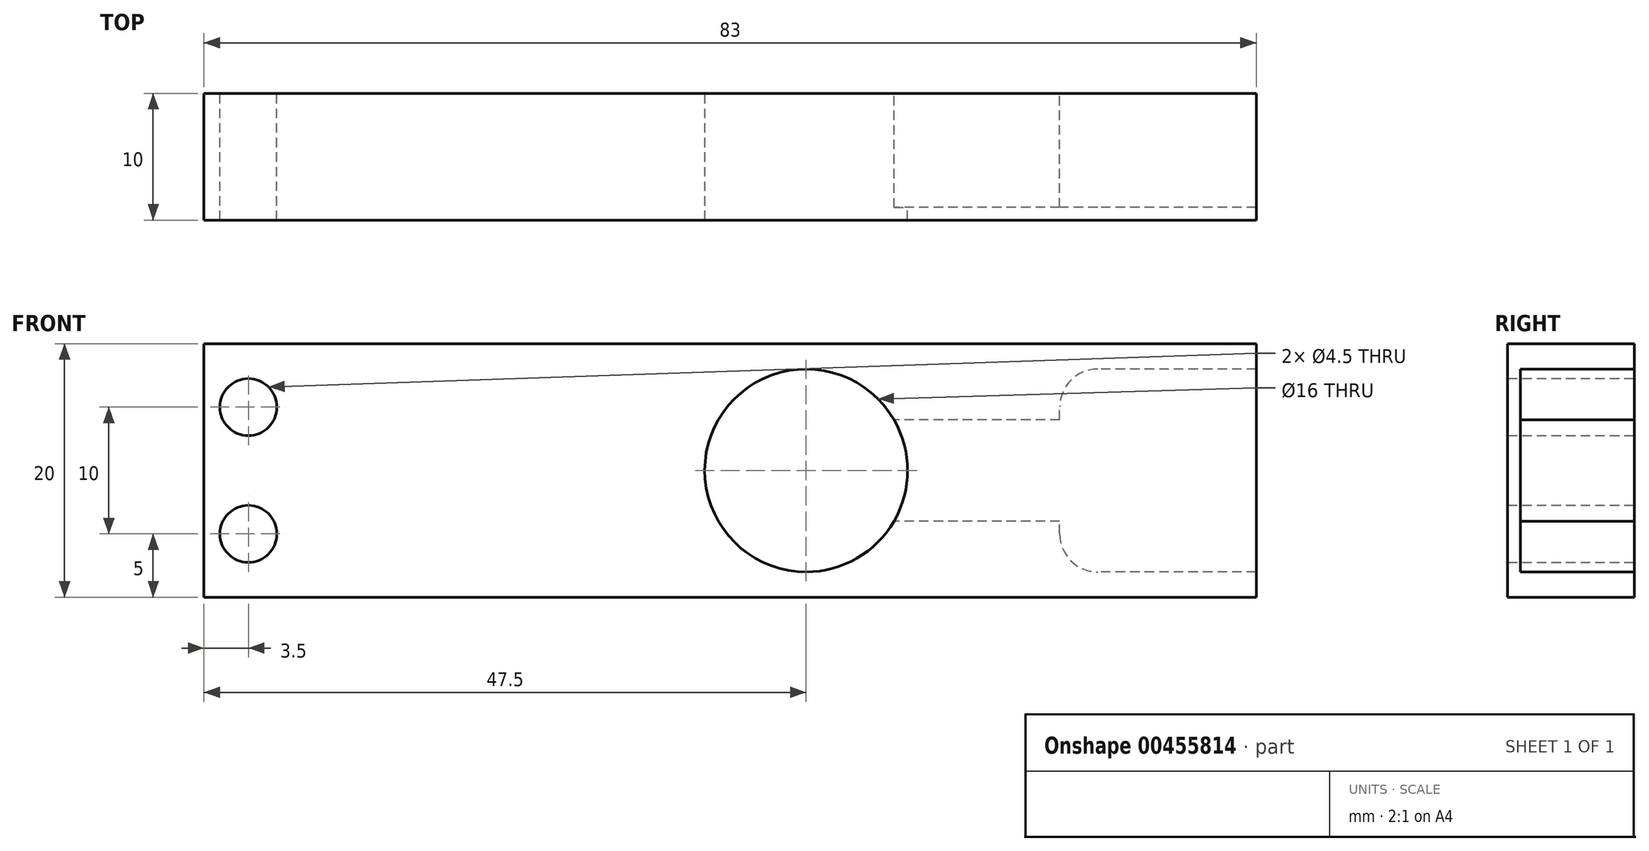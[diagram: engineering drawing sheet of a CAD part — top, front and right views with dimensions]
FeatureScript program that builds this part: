
annotation { "Feature Type Name" : "Feature", "Feature Type Description" : "" }
export const myFeature = defineFeature(function(context is Context, id is Id, definition is map)
    precondition{}
    {
        {
            var Q0;
            Q0=qCreatedBy(makeId("Front.planeOp"),FACE);
            var sketch = newSketch(context, id + "F0", { "sketchPlane" : qUnion([Q0])});
            skLineSegment(sketch, "E0.bottom", {"start": v(-47.5, 10) * mm, "end": v(35.5, 10) * mm});
            skLineSegment(sketch, "E0.top", {"start": v(-47.5, -10) * mm, "end": v(35.5, -10) * mm});
            skLineSegment(sketch, "E0.left", {"start": v(-47.5, 10) * mm, "end": v(-47.5, -10) * mm});
            skLineSegment(sketch, "E0.right", {"start": v(35.5, 10) * mm, "end": v(35.5, -10) * mm});
            skCircle(sketch, "E1", {"center": v(0, 0) * mm, "radius": 8 * mm});
            skCircle(sketch, "E2", {"center": v(-44, 5) * mm, "radius": 2.25 * mm});
            skCircle(sketch, "E3", {"center": v(-44, -5) * mm, "radius": 2.25 * mm});
            skLineSegment(sketch, "E4.bottom", {"start": v(35.5, -8) * mm, "end": v(23, -8) * mm});
            skLineSegment(sketch, "E4.top", {"start": v(35.5, 8) * mm, "end": v(23, 8) * mm});
            skLineSegment(sketch, "E4.left", {"start": v(35.5, -8) * mm, "end": v(35.5, 8) * mm});
            skArc(sketch, "E5", {"start": v(23, -8) * mm, "mid": v(20.88, -7.12) * mm, "end": v(20, -5) * mm});
            skArc(sketch, "E6", {"start": v(23, 8) * mm, "mid": v(20.88, 7.12) * mm, "end": v(20, 5) * mm});
            skLineSegment(sketch, "E7", {"start": v(20, -5) * mm, "end": v(20, -4) * mm});
            skLineSegment(sketch, "E8", {"start": v(35.5, 0) * mm, "end": v(-52.95, 0) * mm, "construction": true});
            skPoint(sketch, "E8.endSnap0", {"position": v(-47.5, 0) * mm});
            skLineSegment(sketch, "E9.bottom", {"start": v(20, -4) * mm, "end": v(6.93, -4) * mm});
            skLineSegment(sketch, "E9.top", {"start": v(20, 4) * mm, "end": v(6.93, 4) * mm});
            skLineSegment(sketch, "E10.trimOffspring", {"start": v(20, 4) * mm, "end": v(20, 5) * mm});
            skSolve(sketch);
        }
        {
            var Q0;
            Q0=makeQuery(id+"F0.imprint","IMPRINT",FACE,{"disambiguationData":[TD([[makeQuery(id+"F0.imprint","IMPRINT",EDGE,{"derivedFrom":sQuery(id+"F0.wireOp",EDGE,"E0.bottom")}),-1.0]])]});
            var Q1;
            Q1=makeQuery(id+"F0.imprint","IMPRINT",FACE,{"disambiguationData":[TD([[makeQuery(id+"F0.imprint","IMPRINT",EDGE,{"derivedFrom":sQuery(id+"F0.wireOp",EDGE,"E4.bottom")}),-1.0]])]});
            extrude(context, id + "F1", {"entities" : qUnion([Q0, Q1]), "depth" : 10 * mm});
        }
        {
            var Q0;
            Q0=makeQuery(id+"F0.imprint","IMPRINT",FACE,{"disambiguationData":[TD([[makeQuery(id+"F0.imprint","IMPRINT",EDGE,{"derivedFrom":sQuery(id+"F0.wireOp",EDGE,"E4.bottom")}),-1.0]])]});
            extrude(context, id + "F2", {"entities" : qUnion([Q0]), "operationType" : NewBodyOperationType.REMOVE, "depth" : 9 * mm});
        }
    });
